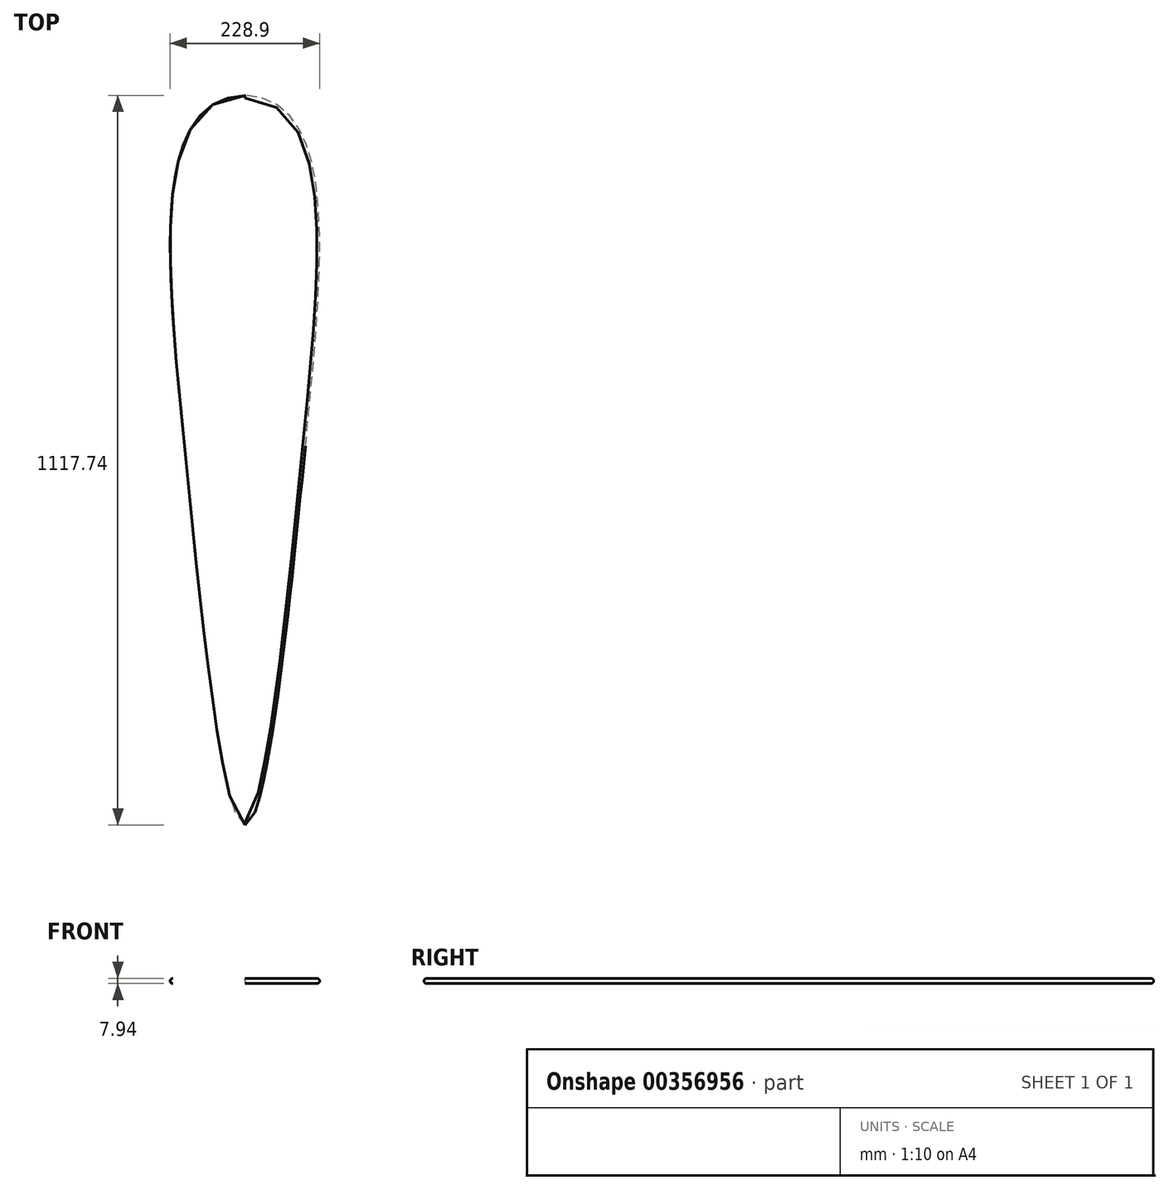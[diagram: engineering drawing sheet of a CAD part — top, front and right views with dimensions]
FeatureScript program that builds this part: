
annotation { "Feature Type Name" : "Feature", "Feature Type Description" : "" }
export const myFeature = defineFeature(function(context is Context, id is Id, definition is map)
    precondition{}
    {
        {
            var Q0;
            Q0=qCreatedBy(makeId("Top.planeOp"),FACE);
            var sketch = newSketch(context, id + "F0", { "sketchPlane" : qUnion([Q0])});
            skLineSegment(sketch, "E0", {"start": v(0, 0) * mm, "end": v(0, 508) * mm});
            skLineSegment(sketch, "E1", {"start": v(0, 508) * mm, "end": v(0, 0) * mm});
            skLineSegment(sketch, "E2", {"start": v(0, 0) * mm, "end": v(0, -609.6) * mm});
            skLineSegment(sketch, "E3", {"start": v(0, 0) * mm, "end": v(88.9, 0) * mm});
            skLineSegment(sketch, "E4", {"start": v(88.9, 0) * mm, "end": v(0, 0) * mm});
            skLineSegment(sketch, "E5", {"start": v(0, 0) * mm, "end": v(-88.9, 0) * mm});
            skSolve(sketch);
        }
        {
            var Q0;
            Q0=qCreatedBy(makeId("Top.planeOp"),FACE);
            var sketch = newSketch(context, id + "F1", { "sketchPlane" : qUnion([Q0])});
            skFitSpline(sketch, "E6", {"points": [v(0, -609.2) * mm, v(95.49, 0) * mm, v(0, 508.53) * mm], "startDerivative": vector(199.85, 0) * mm, "endDerivative": vector(-900.34, 37.9) * mm});
            skFitSpline(sketch, "E7.MirrorCS", {"points": [v(0, -609.2) * mm, v(-95.49, 0) * mm, v(0, 508.53) * mm], "startDerivative": vector(-199.85, 0) * mm, "endDerivative": vector(900.34, 37.9) * mm});
            skSolve(sketch);
        }
        {
            var Q0;
            Q0=makeQuery(id+"F1.imprint","IMPRINT",FACE,{"disambiguationData":[TD([[makeQuery(id+"F1.imprint","IMPRINT",EDGE,{"derivedFrom":sQuery(id+"F1.wireOp",EDGE,"E6")}),1.0]])]});
            extrude(context, id + "F2", {"entities" : qUnion([Q0]), "endBound" : BoundingType.SYMMETRIC, "oppositeDirection" : true, "depth" : 7.94 * mm});
        }
        {
            var Q0;
            Q0=makeQuery(id+"F2.opExtrude","CAP_EDGE",EDGE,{"disambiguationData":[OSD([sQuery(id+"F1.wireOp",EDGE,"E6")])],"isStart":true});
            var Q1;
            Q1=makeQuery(id+"F2.opExtrude","CAP_EDGE",EDGE,{"disambiguationData":[OSD([sQuery(id+"F1.wireOp",EDGE,"E6")])],"isStart":false});
            fillet(context, id + "F3", {"entities" : qUnion([Q0, Q1]), "radius" : 3.96 * mm, "tangentPropagation" : true, "allowEdgeOverflow" : false});
        }
    });
